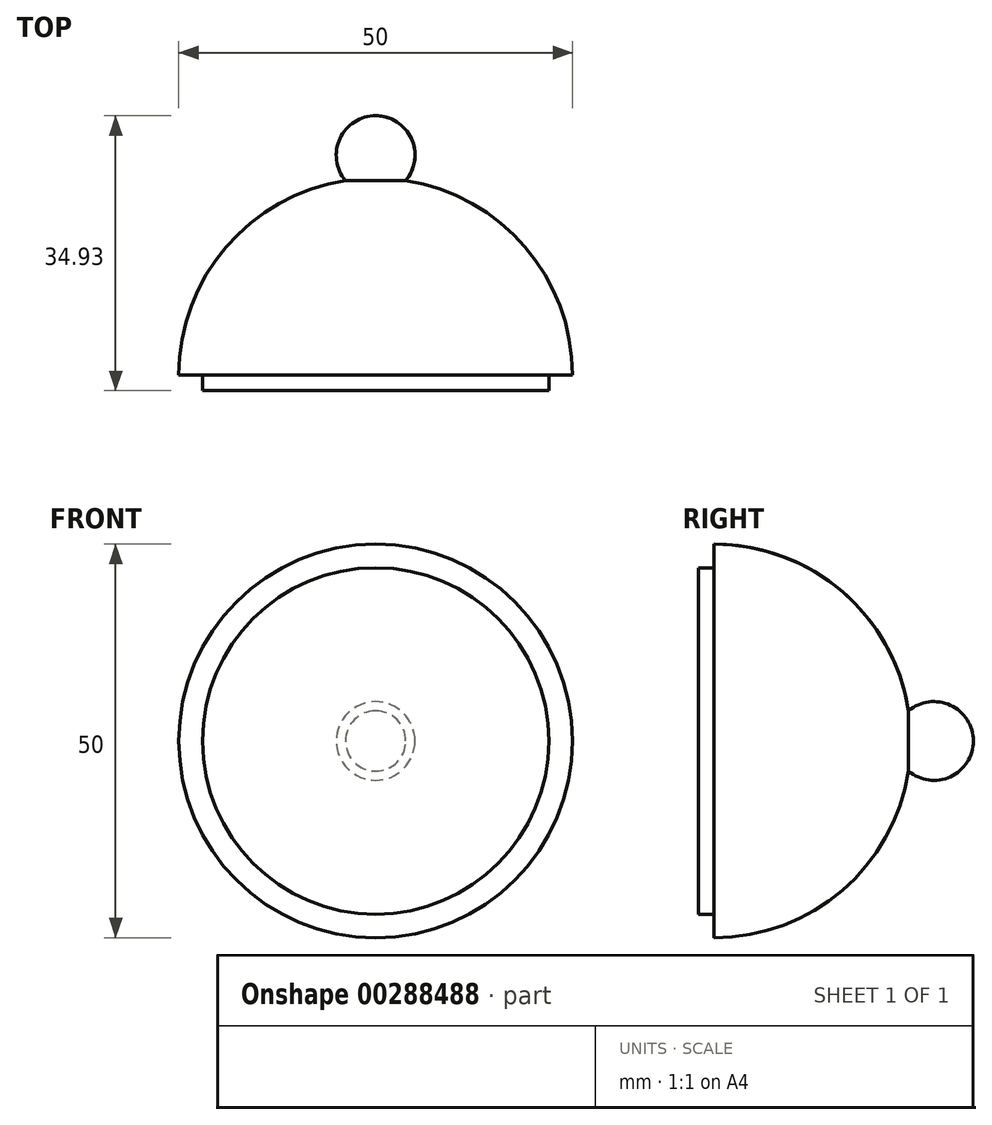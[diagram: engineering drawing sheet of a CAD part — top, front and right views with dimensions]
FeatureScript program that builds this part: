
annotation { "Feature Type Name" : "Feature", "Feature Type Description" : "" }
export const myFeature = defineFeature(function(context is Context, id is Id, definition is map)
    precondition{}
    {
        {
            var Q0;
            Q0=qCreatedBy(makeId("Top.planeOp"),FACE);
            var sketch = newSketch(context, id + "F0", { "sketchPlane" : qUnion([Q0])});
            skArc(sketch, "E0", {"start": v(25, 0) * mm, "mid": v(18.98, 16.27) * mm, "end": v(3.83, 24.7) * mm});
            skArc(sketch, "E1", {"start": v(3.83, 24.7) * mm, "mid": v(4.53, 30.04) * mm, "end": v(0, 32.93) * mm});
            skLineSegment(sketch, "E2", {"start": v(0, 32.93) * mm, "end": v(0, 0) * mm});
            skLineSegment(sketch, "E3", {"start": v(25, 0) * mm, "end": v(22, 0) * mm});
            skPoint(sketch, "E4.orphan", {"position": v(0, 25) * mm});
            skLineSegment(sketch, "E5", {"start": v(22, 0) * mm, "end": v(22, -2) * mm});
            skLineSegment(sketch, "E6", {"start": v(22, -2) * mm, "end": v(0, -2) * mm});
            skLineSegment(sketch, "E7", {"start": v(0, -2) * mm, "end": v(0, 0) * mm});
            skSolve(sketch);
        }
        {
            var Q0;
            Q0=makeQuery(id+"F0.imprint","IMPRINT",FACE,{"disambiguationData":[TD([[makeQuery(id+"F0.imprint","IMPRINT",EDGE,{"derivedFrom":sQuery(id+"F0.wireOp",EDGE,"E0")}),1.0]])]});
            var Q1;
            Q1=sQuery(id+"F0.wireOp",EDGE,"E2");
            revolve(context, id + "F1", {"entities" : qUnion([Q0]), "axis" : qUnion([Q1]), "revolveType" : RevolveType.FULL});
        }
    });
